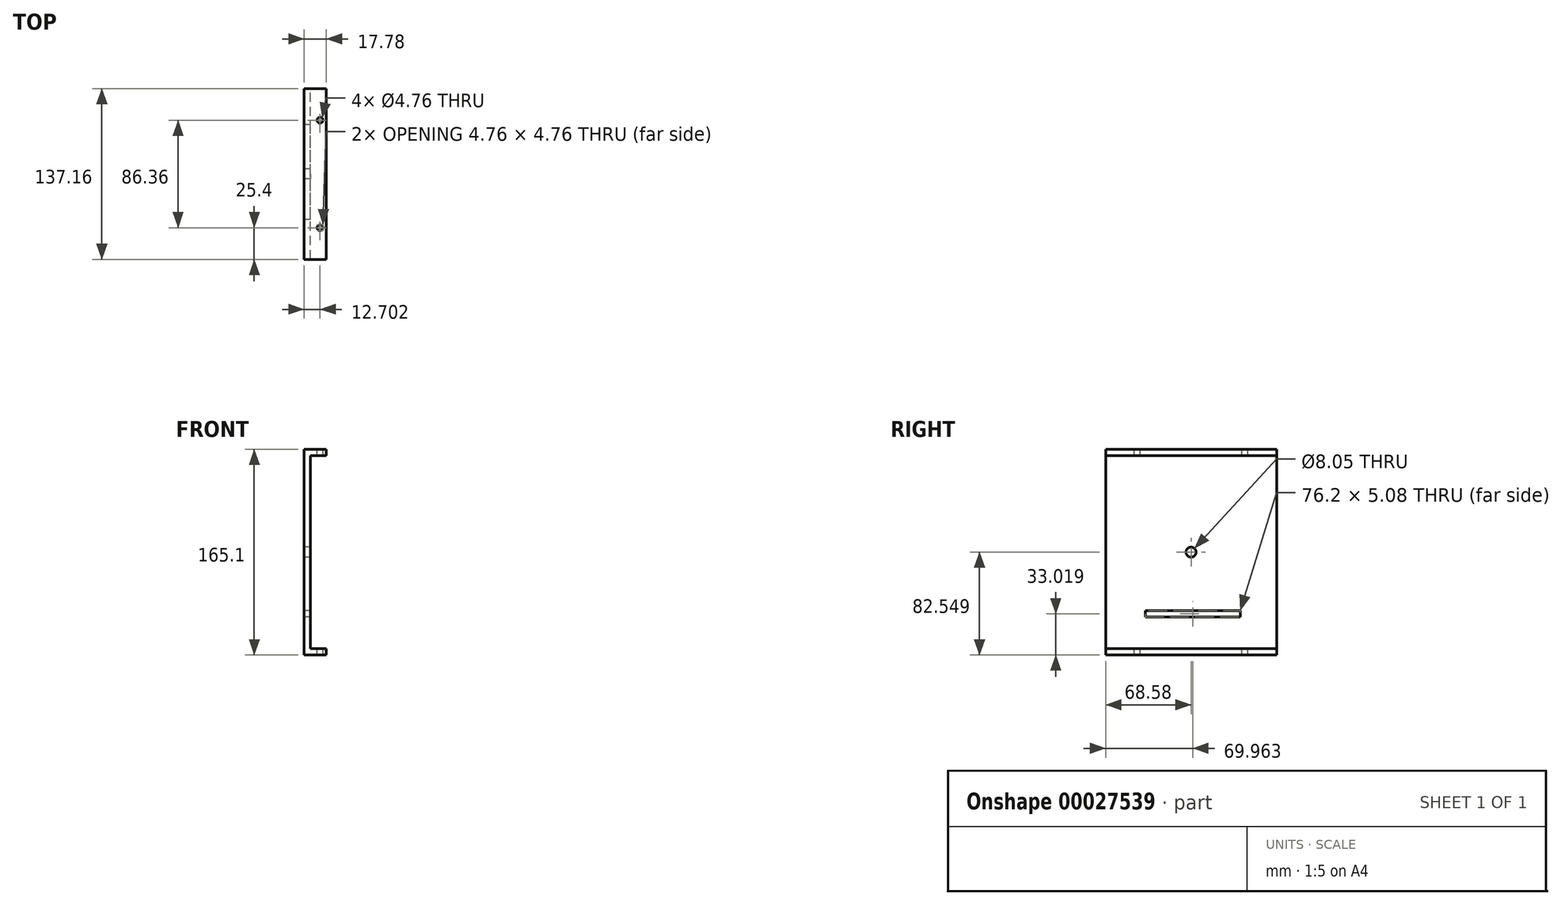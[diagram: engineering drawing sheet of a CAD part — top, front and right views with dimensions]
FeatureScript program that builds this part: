
annotation { "Feature Type Name" : "Feature", "Feature Type Description" : "" }
export const myFeature = defineFeature(function(context is Context, id is Id, definition is map)
    precondition{}
    {
        {
            var Q0;
            Q0=qCreatedBy(makeId("Front.planeOp"),FACE);
            var sketch = newSketch(context, id + "F0", { "sketchPlane" : qUnion([Q0])});
            skLineSegment(sketch, "E0", {"start": v(-33.65, -108.75) * mm, "end": v(-33.65, 56.35) * mm});
            skLineSegment(sketch, "E1", {"start": v(-33.65, 56.35) * mm, "end": v(-15.87, 56.35) * mm});
            skLineSegment(sketch, "E2", {"start": v(-15.87, 56.35) * mm, "end": v(-15.87, 51.27) * mm});
            skLineSegment(sketch, "E3", {"start": v(-15.87, 51.27) * mm, "end": v(-28.57, 51.27) * mm});
            skLineSegment(sketch, "E4", {"start": v(-28.57, 51.27) * mm, "end": v(-28.57, -103.67) * mm});
            skLineSegment(sketch, "E5", {"start": v(-28.57, -103.67) * mm, "end": v(-15.87, -103.67) * mm});
            skLineSegment(sketch, "E6", {"start": v(-15.87, -103.67) * mm, "end": v(-15.87, -108.75) * mm});
            skLineSegment(sketch, "E7", {"start": v(-15.87, -108.75) * mm, "end": v(-33.65, -108.75) * mm});
            skSolve(sketch);
        }
        {
            var Q0;
            Q0=makeQuery(id+"F0.imprint","IMPRINT",FACE,{"disambiguationData":[TD([[makeQuery(id+"F0.imprint","IMPRINT",EDGE,{"derivedFrom":sQuery(id+"F0.wireOp",EDGE,"E0")}),-1.0]])]});
            extrude(context, id + "F1", {"entities" : qUnion([Q0]), "depth" : 137.16 * mm});
        }
        {
            var Q0;
            Q0=makeQuery(id+"F1.opExtrude","SWEPT_FACE",FACE,{"disambiguationData":[OSD([sQuery(id+"F0.wireOp",EDGE,"E0")])]});
            var sketch = newSketch(context, id + "F2", { "sketchPlane" : qUnion([Q0])});
            skCircle(sketch, "E8", {"center": v(68.58, -26.2) * mm, "radius": 4.03 * mm});
            skPoint(sketch, "E8.centerSnap0", {"position": v(68.58, 56.35) * mm});
            skPoint(sketch, "E8.centerSnap1", {"position": v(0, -26.2) * mm});
            skLineSegment(sketch, "E9.bottom", {"start": v(29.1, -73.2) * mm, "end": v(105.3, -73.2) * mm});
            skLineSegment(sketch, "E9.top", {"start": v(29.1, -78.27) * mm, "end": v(105.3, -78.27) * mm});
            skLineSegment(sketch, "E9.left", {"start": v(29.1, -73.2) * mm, "end": v(29.1, -78.27) * mm});
            skLineSegment(sketch, "E9.right", {"start": v(105.3, -73.2) * mm, "end": v(105.3, -78.27) * mm});
            skSolve(sketch);
        }
        {
            var Q0;
            Q0=makeQuery(id+"F2.imprint","IMPRINT",FACE,{"disambiguationData":[TD([[makeQuery(id+"F2.imprint","IMPRINT",EDGE,{"derivedFrom":sQuery(id+"F2.wireOp",EDGE,"E8")}),1.0]])]});
            var Q1;
            Q1=makeQuery(id+"F2.imprint","IMPRINT",FACE,{"disambiguationData":[TD([[makeQuery(id+"F2.imprint","IMPRINT",EDGE,{"derivedFrom":sQuery(id+"F2.wireOp",EDGE,"E9.bottom")}),-1.0]])]});
            extrude(context, id + "F3", {"entities" : qUnion([Q0, Q1]), "operationType" : NewBodyOperationType.REMOVE, "oppositeDirection" : true, "depth" : 7.62 * mm});
        }
        {
            var Q0;
            Q0=makeQuery(id+"F1.opExtrude","SWEPT_FACE",FACE,{"disambiguationData":[OSD([sQuery(id+"F0.wireOp",EDGE,"E1")])]});
            var sketch = newSketch(context, id + "F4", { "sketchPlane" : qUnion([Q0])});
            skLineSegment(sketch, "E10", {"start": v(-15.87, 0) * mm, "end": v(-20.95, 0) * mm});
            skLineSegment(sketch, "E11", {"start": v(-20.95, 0) * mm, "end": v(-20.95, -25.4) * mm});
            skLineSegment(sketch, "E12", {"start": v(-15.87, -137.16) * mm, "end": v(-20.95, -137.16) * mm});
            skLineSegment(sketch, "E13", {"start": v(-20.95, -137.16) * mm, "end": v(-20.95, -111.76) * mm});
            skCircle(sketch, "E14", {"center": v(-20.95, -111.76) * mm, "radius": 2.38 * mm});
            skCircle(sketch, "E15", {"center": v(-20.95, -25.4) * mm, "radius": 2.38 * mm});
            skSolve(sketch);
        }
        {
            var Q0;
            Q0=makeQuery(id+"F4.imprint","IMPRINT",FACE,{"disambiguationData":[TD([[makeQuery(id+"F4.imprint","IMPRINT",EDGE,{"derivedFrom":sQuery(id+"F4.wireOp",EDGE,"E15")}),1.0]])]});
            var Q1;
            Q1=makeQuery(id+"F4.imprint","IMPRINT",FACE,{"disambiguationData":[TD([[makeQuery(id+"F4.imprint","IMPRINT",EDGE,{"derivedFrom":sQuery(id+"F4.wireOp",EDGE,"E14")}),1.0]])]});
            extrude(context, id + "F5", {"entities" : qUnion([Q0, Q1]), "operationType" : NewBodyOperationType.REMOVE, "oppositeDirection" : true, "depth" : 254 * mm});
        }
    });
